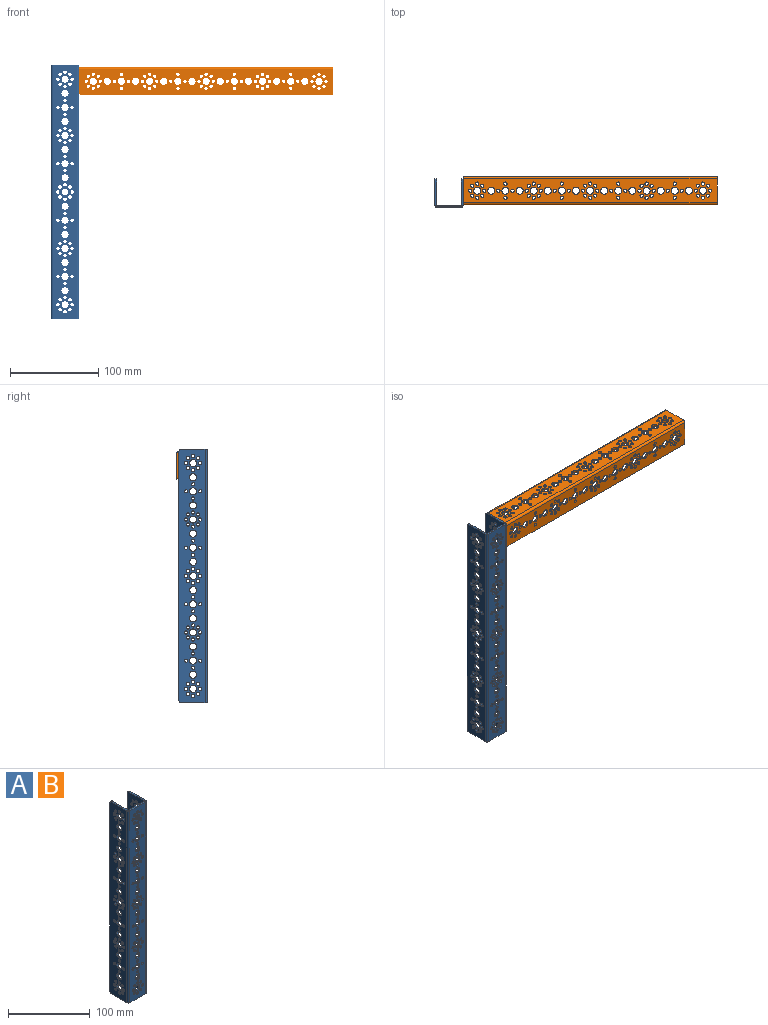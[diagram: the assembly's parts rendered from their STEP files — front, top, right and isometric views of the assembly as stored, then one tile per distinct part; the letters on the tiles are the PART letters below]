
ASSEMBLY  parts=2 mates=1
PART A: 237 faces, bbox 32x32x288 mm
  f0: plane 288x29.5mm, normal (1,0,0), area 7036.7mm2, adj f7,f8,f12,f13,f14,f17,f20,f22
  f1: plane 288x29.5mm, normal (-1,0,0), area 7036.7mm2, adj f8,f9,f12,f13,f14,f17,f20,f22
  f2: plane 288x29.5mm, normal (1,0,0), area 7036.7mm2, adj f10,f11,f12,f13,f15,f16,f19,f21
  f3: plane 288x29.5mm, normal (-1,0,0), area 7036.7mm2, adj f6,f11,f12,f13,f15,f16,f19,f21
  f4: plane 288x27mm, normal (0,-1,0), area 6319.4mm2, adj f6,f7,f12,f13,f18,f23,f24,f25
  f5: plane 288x27mm, normal (0,1,0), area 6319.4mm2, adj f9,f10,f12,f13,f18,f23,f24,f25
  f6: cylinder r=2.5mm len=288mm, axis (0,0,-1), area 1131mm2, adj f3,f4,f12,f13
  f7: cylinder r=2.5mm len=288mm, axis (0,0,-1), area 1131mm2, adj f0,f4,f12,f13
  f8: plane 283x2mm, normal (0,1,0), area 566mm2, adj f0,f1,f14,f17
  f9: cylinder r=0.5mm len=288mm, axis (0,0,-1), area 226.2mm2, adj f1,f5,f12,f13
  f10: cylinder r=0.5mm len=288mm, axis (0,0,-1), area 226.2mm2, adj f2,f5,f12,f13
  f11: plane 283x2mm, normal (0,1,0), area 566mm2, adj f2,f3,f15,f16
  f12: plane 32x29.5mm, normal (0,0,1), area 171.4mm2, adj f0,f1,f2,f3,f4,f5,f6,f7
  f13: plane 32x29.5mm, normal (0,0,-1), area 171.4mm2, adj f0,f1,f2,f3,f4,f5,f6,f7
  f14: cylinder r=2.5mm len=2.5mm, axis (1,0,0), area 7.9mm2, adj f0,f1,f8,f12
  f15: cylinder r=2.5mm len=2.5mm, axis (1,0,0), area 7.9mm2, adj f2,f3,f11,f12
  f16: cylinder r=2.5mm len=2.5mm, axis (-1,0,0), area 7.9mm2, adj f2,f3,f11,f13
  f17: cylinder r=2.5mm len=2.5mm, axis (-1,0,0), area 7.9mm2, adj f0,f1,f8,f13
  f18: cylinder r=4mm len=8mm, axis (0,-1,0), area 50.3mm2, adj f4,f5
  f19: cylinder r=4mm len=8mm, axis (-1,0,0), area 50.3mm2, adj f2,f3
  f20: cylinder r=4mm len=8mm, axis (-1,0,0), area 50.3mm2, adj f0,f1
  f21: cylinder r=1.85mm len=3.7mm, axis (-1,0,0), area 23.2mm2, adj f2,f3
  f22: cylinder r=1.85mm len=3.7mm, axis (-1,0,0), area 23.2mm2, adj f0,f1
  f23: cylinder r=1.85mm len=3.7mm, axis (0,-1,0), area 23.2mm2, adj f4,f5
  f24: cylinder r=4mm len=8mm, axis (0,-1,0), area 50.3mm2, adj f4,f5
  f25: cylinder r=4mm len=8mm, axis (0,-1,0), area 50.3mm2, adj f4,f5
  f26: cylinder r=4mm len=8mm, axis (0,-1,0), area 50.3mm2, adj f4,f5
  f27: cylinder r=4mm len=8mm, axis (0,-1,0), area 50.3mm2, adj f4,f5
  f28: cylinder r=4mm len=8mm, axis (0,-1,0), area 50.3mm2, adj f4,f5
  f29: cylinder r=4mm len=8mm, axis (0,-1,0), area 50.3mm2, adj f4,f5
  f30: cylinder r=4mm len=8mm, axis (0,-1,0), area 50.3mm2, adj f4,f5
  f31: cylinder r=4mm len=8mm, axis (0,-1,0), area 50.3mm2, adj f4,f5
  f32: cylinder r=4mm len=8mm, axis (0,-1,0), area 50.3mm2, adj f4,f5
  f33: cylinder r=4mm len=8mm, axis (0,-1,0), area 50.3mm2, adj f4,f5
  f34: cylinder r=4mm len=8mm, axis (0,-1,0), area 50.3mm2, adj f4,f5
  f35: cylinder r=4mm len=8mm, axis (0,-1,0), area 50.3mm2, adj f4,f5
  f36: cylinder r=4mm len=8mm, axis (0,-1,0), area 50.3mm2, adj f4,f5
  f37: cylinder r=4mm len=8mm, axis (0,-1,0), area 50.3mm2, adj f4,f5
  f38: cylinder r=4mm len=8mm, axis (0,-1,0), area 50.3mm2, adj f4,f5
  f39: cylinder r=4mm len=8mm, axis (0,-1,0), area 50.3mm2, adj f4,f5
  f40: cylinder r=4mm len=8mm, axis (-1,0,0), area 50.3mm2, adj f2,f3
  f41: cylinder r=4mm len=8mm, axis (-1,0,0), area 50.3mm2, adj f0,f1
  f42: cylinder r=4mm len=8mm, axis (-1,0,0), area 50.3mm2, adj f2,f3
  f43: cylinder r=4mm len=8mm, axis (-1,0,0), area 50.3mm2, adj f0,f1
  f44: cylinder r=4mm len=8mm, axis (-1,0,0), area 50.3mm2, adj f2,f3
  f45: cylinder r=4mm len=8mm, axis (-1,0,0), area 50.3mm2, adj f0,f1
  f46: cylinder r=4mm len=8mm, axis (-1,0,0), area 50.3mm2, adj f2,f3
  f47: cylinder r=4mm len=8mm, axis (-1,0,0), area 50.3mm2, adj f0,f1
  f48: cylinder r=4mm len=8mm, axis (-1,0,0), area 50.3mm2, adj f2,f3
  f49: cylinder r=4mm len=8mm, axis (-1,0,0), area 50.3mm2, adj f0,f1
  f50: cylinder r=4mm len=8mm, axis (-1,0,0), area 50.3mm2, adj f2,f3
  f51: cylinder r=4mm len=8mm, axis (-1,0,0), area 50.3mm2, adj f0,f1
  f52: cylinder r=4mm len=8mm, axis (-1,0,0), area 50.3mm2, adj f2,f3
  f53: cylinder r=4mm len=8mm, axis (-1,0,0), area 50.3mm2, adj f0,f1
  f54: cylinder r=4mm len=8mm, axis (-1,0,0), area 50.3mm2, adj f2,f3
  f55: cylinder r=4mm len=8mm, axis (-1,0,0), area 50.3mm2, adj f0,f1
  f56: cylinder r=4mm len=8mm, axis (-1,0,0), area 50.3mm2, adj f2,f3
  f57: cylinder r=4mm len=8mm, axis (-1,0,0), area 50.3mm2, adj f0,f1
  f58: cylinder r=4mm len=8mm, axis (-1,0,0), area 50.3mm2, adj f2,f3
  f59: cylinder r=4mm len=8mm, axis (-1,0,0), area 50.3mm2, adj f0,f1
  f60: cylinder r=4mm len=8mm, axis (-1,0,0), area 50.3mm2, adj f2,f3
  f61: cylinder r=4mm len=8mm, axis (-1,0,0), area 50.3mm2, adj f0,f1
  f62: cylinder r=4mm len=8mm, axis (-1,0,0), area 50.3mm2, adj f2,f3
  f63: cylinder r=4mm len=8mm, axis (-1,0,0), area 50.3mm2, adj f0,f1
  f64: cylinder r=4mm len=8mm, axis (-1,0,0), area 50.3mm2, adj f2,f3
  f65: cylinder r=4mm len=8mm, axis (-1,0,0), area 50.3mm2, adj f0,f1
  f66: cylinder r=4mm len=8mm, axis (-1,0,0), area 50.3mm2, adj f2,f3
  f67: cylinder r=4mm len=8mm, axis (-1,0,0), area 50.3mm2, adj f0,f1
  f68: cylinder r=4mm len=8mm, axis (-1,0,0), area 50.3mm2, adj f2,f3
  f69: cylinder r=4mm len=8mm, axis (-1,0,0), area 50.3mm2, adj f0,f1
  f70: cylinder r=4mm len=8mm, axis (-1,0,0), area 50.3mm2, adj f2,f3
  f71: cylinder r=4mm len=8mm, axis (-1,0,0), area 50.3mm2, adj f0,f1
  f72: cylinder r=1.85mm len=3.7mm, axis (0,-1,0), area 23.2mm2, adj f4,f5
  f73: cylinder r=1.85mm len=3.7mm, axis (0,-1,0), area 23.2mm2, adj f4,f5
  f74: cylinder r=1.85mm len=3.7mm, axis (0,-1,0), area 23.2mm2, adj f4,f5
  f75: cylinder r=1.85mm len=3.7mm, axis (0,-1,0), area 23.2mm2, adj f4,f5
  f76: cylinder r=1.85mm len=3.7mm, axis (0,-1,0), area 23.2mm2, adj f4,f5
  f77: cylinder r=1.85mm len=3.7mm, axis (0,-1,0), area 23.2mm2, adj f4,f5
  f78: cylinder r=1.85mm len=3.7mm, axis (0,-1,0), area 23.2mm2, adj f4,f5
  f79: cylinder r=1.85mm len=3.7mm, axis (-1,0,0), area 23.2mm2, adj f2,f3
  f80: cylinder r=1.85mm len=3.7mm, axis (-1,0,0), area 23.2mm2, adj f0,f1
  f81: cylinder r=1.85mm len=3.7mm, axis (-1,0,0), area 23.2mm2, adj f2,f3
  f82: cylinder r=1.85mm len=3.7mm, axis (-1,0,0), area 23.2mm2, adj f0,f1
  f83: cylinder r=1.85mm len=3.7mm, axis (-1,0,0), area 23.2mm2, adj f2,f3
  f84: cylinder r=1.85mm len=3.7mm, axis (-1,0,0), area 23.2mm2, adj f0,f1
  f85: cylinder r=1.85mm len=3.7mm, axis (-1,0,0), area 23.2mm2, adj f2,f3
  f86: cylinder r=1.85mm len=3.7mm, axis (-1,0,0), area 23.2mm2, adj f0,f1
  f87: cylinder r=1.85mm len=3.7mm, axis (-1,0,0), area 23.2mm2, adj f2,f3
  f88: cylinder r=1.85mm len=3.7mm, axis (-1,0,0), area 23.2mm2, adj f0,f1
  f89: cylinder r=1.85mm len=3.7mm, axis (-1,0,0), area 23.2mm2, adj f2,f3
  f90: cylinder r=1.85mm len=3.7mm, axis (-1,0,0), area 23.2mm2, adj f0,f1
  f91: cylinder r=1.85mm len=3.7mm, axis (-1,0,0), area 23.2mm2, adj f2,f3
  f92: cylinder r=1.85mm len=3.7mm, axis (-1,0,0), area 23.2mm2, adj f0,f1
  f93: cylinder r=1.85mm len=3.7mm, axis (0,-1,0), area 23.2mm2, adj f4,f5
  f94: cylinder r=1.85mm len=3.7mm, axis (-1,0,0), area 23.2mm2, adj f2,f3
  f95: cylinder r=1.85mm len=3.7mm, axis (-1,0,0), area 23.2mm2, adj f0,f1
  f96: cylinder r=1.85mm len=3.7mm, axis (0,-1,0), area 23.2mm2, adj f4,f5
  f97: cylinder r=1.85mm len=3.7mm, axis (0,-1,0), area 23.2mm2, adj f4,f5
  f98: cylinder r=1.85mm len=3.7mm, axis (0,-1,0), area 23.2mm2, adj f4,f5
  f99: cylinder r=1.85mm len=3.7mm, axis (-1,0,0), area 23.2mm2, adj f2,f3
  f100: cylinder r=1.85mm len=3.7mm, axis (-1,0,0), area 23.2mm2, adj f0,f1
  f101: cylinder r=1.85mm len=3.7mm, axis (-1,0,0), area 23.2mm2, adj f2,f3
  f102: cylinder r=1.85mm len=3.7mm, axis (-1,0,0), area 23.2mm2, adj f0,f1
  f103: cylinder r=1.85mm len=3.7mm, axis (-1,0,0), area 23.2mm2, adj f2,f3
  f104: cylinder r=1.85mm len=3.7mm, axis (-1,0,0), area 23.2mm2, adj f0,f1
  f105: cylinder r=1.85mm len=3.7mm, axis (0,-1,0), area 23.2mm2, adj f4,f5
  f106: cylinder r=1.85mm len=3.7mm, axis (0,-1,0), area 23.2mm2, adj f4,f5
  f107: cylinder r=1.85mm len=3.7mm, axis (0,-1,0), area 23.2mm2, adj f4,f5
  f108: cylinder r=1.85mm len=3.7mm, axis (0,-1,0), area 23.2mm2, adj f4,f5
  f109: cylinder r=1.85mm len=3.7mm, axis (0,-1,0), area 23.2mm2, adj f4,f5
  f110: cylinder r=1.85mm len=3.7mm, axis (0,-1,0), area 23.2mm2, adj f4,f5
  f111: cylinder r=1.85mm len=3.7mm, axis (0,-1,0), area 23.2mm2, adj f4,f5
  f112: cylinder r=1.85mm len=3.7mm, axis (0,-1,0), area 23.2mm2, adj f4,f5
  f113: cylinder r=1.85mm len=3.7mm, axis (0,-1,0), area 23.2mm2, adj f4,f5
  f114: cylinder r=1.85mm len=3.7mm, axis (0,-1,0), area 23.2mm2, adj f4,f5
  f115: cylinder r=1.85mm len=3.7mm, axis (0,-1,0), area 23.2mm2, adj f4,f5
  f116: cylinder r=1.85mm len=3.7mm, axis (0,-1,0), area 23.2mm2, adj f4,f5
  f117: cylinder r=1.85mm len=3.7mm, axis (0,-1,0), area 23.2mm2, adj f4,f5
  f118: cylinder r=1.85mm len=3.7mm, axis (0,-1,0), area 23.2mm2, adj f4,f5
  f119: cylinder r=1.85mm len=3.7mm, axis (0,-1,0), area 23.2mm2, adj f4,f5
  f120: cylinder r=1.85mm len=3.7mm, axis (0,-1,0), area 23.2mm2, adj f4,f5
  f121: cylinder r=1.85mm len=3.7mm, axis (-1,0,0), area 23.2mm2, adj f2,f3
  f122: cylinder r=1.85mm len=3.7mm, axis (-1,0,0), area 23.2mm2, adj f0,f1
  f123: cylinder r=1.85mm len=3.7mm, axis (-1,0,0), area 23.2mm2, adj f2,f3
  f124: cylinder r=1.85mm len=3.7mm, axis (-1,0,0), area 23.2mm2, adj f0,f1
  f125: cylinder r=1.85mm len=3.7mm, axis (-1,0,0), area 23.2mm2, adj f2,f3
  f126: cylinder r=1.85mm len=3.7mm, axis (-1,0,0), area 23.2mm2, adj f0,f1
  f127: cylinder r=1.85mm len=3.7mm, axis (-1,0,0), area 23.2mm2, adj f2,f3
  f128: cylinder r=1.85mm len=3.7mm, axis (-1,0,0), area 23.2mm2, adj f0,f1
  f129: cylinder r=1.85mm len=3.7mm, axis (-1,0,0), area 23.2mm2, adj f2,f3
  f130: cylinder r=1.85mm len=3.7mm, axis (-1,0,0), area 23.2mm2, adj f0,f1
  f131: cylinder r=1.85mm len=3.7mm, axis (-1,0,0), area 23.2mm2, adj f2,f3
  f132: cylinder r=1.85mm len=3.7mm, axis (-1,0,0), area 23.2mm2, adj f0,f1
  f133: cylinder r=1.85mm len=3.7mm, axis (-1,0,0), area 23.2mm2, adj f2,f3
  f134: cylinder r=1.85mm len=3.7mm, axis (-1,0,0), area 23.2mm2, adj f0,f1
  f135: cylinder r=1.85mm len=3.7mm, axis (-1,0,0), area 23.2mm2, adj f2,f3
  f136: cylinder r=1.85mm len=3.7mm, axis (-1,0,0), area 23.2mm2, adj f0,f1
  f137: cylinder r=1.85mm len=3.7mm, axis (-1,0,0), area 23.2mm2, adj f2,f3
  f138: cylinder r=1.85mm len=3.7mm, axis (-1,0,0), area 23.2mm2, adj f0,f1
  f139: cylinder r=1.85mm len=3.7mm, axis (-1,0,0), area 23.2mm2, adj f2,f3
  f140: cylinder r=1.85mm len=3.7mm, axis (-1,0,0), area 23.2mm2, adj f0,f1
  f141: cylinder r=1.85mm len=3.7mm, axis (-1,0,0), area 23.2mm2, adj f2,f3
  f142: cylinder r=1.85mm len=3.7mm, axis (-1,0,0), area 23.2mm2, adj f0,f1
  f143: cylinder r=1.85mm len=3.7mm, axis (-1,0,0), area 23.2mm2, adj f2,f3
  f144: cylinder r=1.85mm len=3.7mm, axis (-1,0,0), area 23.2mm2, adj f0,f1
  f145: cylinder r=1.85mm len=3.7mm, axis (-1,0,0), area 23.2mm2, adj f2,f3
  f146: cylinder r=1.85mm len=3.7mm, axis (-1,0,0), area 23.2mm2, adj f0,f1
  f147: cylinder r=1.85mm len=3.7mm, axis (-1,0,0), area 23.2mm2, adj f2,f3
  f148: cylinder r=1.85mm len=3.7mm, axis (-1,0,0), area 23.2mm2, adj f0,f1
  f149: cylinder r=1.85mm len=3.7mm, axis (-1,0,0), area 23.2mm2, adj f2,f3
  f150: cylinder r=1.85mm len=3.7mm, axis (-1,0,0), area 23.2mm2, adj f0,f1
  f151: cylinder r=1.85mm len=3.7mm, axis (-1,0,0), area 23.2mm2, adj f2,f3
  f152: cylinder r=1.85mm len=3.7mm, axis (-1,0,0), area 23.2mm2, adj f0,f1
  f153: cylinder r=1.85mm len=3.7mm, axis (0,-1,0), area 23.2mm2, adj f4,f5
  f154: cylinder r=1.85mm len=3.7mm, axis (0,-1,0), area 23.2mm2, adj f4,f5
  f155: cylinder r=1.85mm len=3.7mm, axis (0,-1,0), area 23.2mm2, adj f4,f5
  f156: cylinder r=1.85mm len=3.7mm, axis (0,-1,0), area 23.2mm2, adj f4,f5
  f157: cylinder r=1.85mm len=3.7mm, axis (-1,0,0), area 23.2mm2, adj f2,f3
  f158: cylinder r=1.85mm len=3.7mm, axis (-1,0,0), area 23.2mm2, adj f0,f1
  f159: cylinder r=1.85mm len=3.7mm, axis (-1,0,0), area 23.2mm2, adj f2,f3
  f160: cylinder r=1.85mm len=3.7mm, axis (-1,0,0), area 23.2mm2, adj f0,f1
  f161: cylinder r=1.85mm len=3.7mm, axis (-1,0,0), area 23.2mm2, adj f2,f3
  f162: cylinder r=1.85mm len=3.7mm, axis (-1,0,0), area 23.2mm2, adj f0,f1
  f163: cylinder r=1.85mm len=3.7mm, axis (-1,0,0), area 23.2mm2, adj f2,f3
  f164: cylinder r=1.85mm len=3.7mm, axis (-1,0,0), area 23.2mm2, adj f0,f1
  f165: cylinder r=1.85mm len=3.7mm, axis (0,-1,0), area 23.2mm2, adj f4,f5
  f166: cylinder r=1.85mm len=3.7mm, axis (0,-1,0), area 23.2mm2, adj f4,f5
  f167: cylinder r=1.85mm len=3.7mm, axis (0,-1,0), area 23.2mm2, adj f4,f5
  f168: cylinder r=1.85mm len=3.7mm, axis (0,-1,0), area 23.2mm2, adj f4,f5
  f169: cylinder r=1.85mm len=3.7mm, axis (0,-1,0), area 23.2mm2, adj f4,f5
  f170: cylinder r=1.85mm len=3.7mm, axis (0,-1,0), area 23.2mm2, adj f4,f5
  f171: cylinder r=1.85mm len=3.7mm, axis (0,-1,0), area 23.2mm2, adj f4,f5
  f172: cylinder r=1.85mm len=3.7mm, axis (0,-1,0), area 23.2mm2, adj f4,f5
  f173: cylinder r=1.85mm len=3.7mm, axis (0,-1,0), area 23.2mm2, adj f4,f5
  f174: cylinder r=1.85mm len=3.7mm, axis (0,-1,0), area 23.2mm2, adj f4,f5
  f175: cylinder r=1.85mm len=3.7mm, axis (0,-1,0), area 23.2mm2, adj f4,f5
  f176: cylinder r=1.85mm len=3.7mm, axis (0,-1,0), area 23.2mm2, adj f4,f5
  f177: cylinder r=1.85mm len=3.7mm, axis (0,-1,0), area 23.2mm2, adj f4,f5
  f178: cylinder r=1.85mm len=3.7mm, axis (0,-1,0), area 23.2mm2, adj f4,f5
  f179: cylinder r=1.85mm len=3.7mm, axis (0,-1,0), area 23.2mm2, adj f4,f5
  f180: cylinder r=1.85mm len=3.7mm, axis (0,-1,0), area 23.2mm2, adj f4,f5
  f181: cylinder r=1.85mm len=3.7mm, axis (-1,0,0), area 23.2mm2, adj f2,f3
  f182: cylinder r=1.85mm len=3.7mm, axis (-1,0,0), area 23.2mm2, adj f0,f1
  f183: cylinder r=1.85mm len=3.7mm, axis (-1,0,0), area 23.2mm2, adj f2,f3
  f184: cylinder r=1.85mm len=3.7mm, axis (-1,0,0), area 23.2mm2, adj f0,f1
  f185: cylinder r=1.85mm len=3.7mm, axis (-1,0,0), area 23.2mm2, adj f2,f3
  f186: cylinder r=1.85mm len=3.7mm, axis (-1,0,0), area 23.2mm2, adj f0,f1
  f187: cylinder r=1.85mm len=3.7mm, axis (-1,0,0), area 23.2mm2, adj f2,f3
  f188: cylinder r=1.85mm len=3.7mm, axis (-1,0,0), area 23.2mm2, adj f0,f1
  f189: cylinder r=1.85mm len=3.7mm, axis (-1,0,0), area 23.2mm2, adj f2,f3
  f190: cylinder r=1.85mm len=3.7mm, axis (-1,0,0), area 23.2mm2, adj f0,f1
  f191: cylinder r=1.85mm len=3.7mm, axis (-1,0,0), area 23.2mm2, adj f2,f3
  f192: cylinder r=1.85mm len=3.7mm, axis (-1,0,0), area 23.2mm2, adj f0,f1
  f193: cylinder r=1.85mm len=3.7mm, axis (-1,0,0), area 23.2mm2, adj f2,f3
  f194: cylinder r=1.85mm len=3.7mm, axis (-1,0,0), area 23.2mm2, adj f0,f1
  f195: cylinder r=1.85mm len=3.7mm, axis (-1,0,0), area 23.2mm2, adj f2,f3
  f196: cylinder r=1.85mm len=3.7mm, axis (-1,0,0), area 23.2mm2, adj f0,f1
  f197: cylinder r=1.85mm len=3.7mm, axis (-1,0,0), area 23.2mm2, adj f2,f3
  f198: cylinder r=1.85mm len=3.7mm, axis (-1,0,0), area 23.2mm2, adj f0,f1
  f199: cylinder r=1.85mm len=3.7mm, axis (-1,0,0), area 23.2mm2, adj f2,f3
  f200: cylinder r=1.85mm len=3.7mm, axis (-1,0,0), area 23.2mm2, adj f0,f1
  f201: cylinder r=1.85mm len=3.7mm, axis (-1,0,0), area 23.2mm2, adj f2,f3
  f202: cylinder r=1.85mm len=3.7mm, axis (-1,0,0), area 23.2mm2, adj f0,f1
  f203: cylinder r=1.85mm len=3.7mm, axis (-1,0,0), area 23.2mm2, adj f2,f3
  f204: cylinder r=1.85mm len=3.7mm, axis (-1,0,0), area 23.2mm2, adj f0,f1
  f205: cylinder r=1.85mm len=3.7mm, axis (-1,0,0), area 23.2mm2, adj f2,f3
  f206: cylinder r=1.85mm len=3.7mm, axis (-1,0,0), area 23.2mm2, adj f0,f1
  f207: cylinder r=1.85mm len=3.7mm, axis (-1,0,0), area 23.2mm2, adj f2,f3
  f208: cylinder r=1.85mm len=3.7mm, axis (-1,0,0), area 23.2mm2, adj f0,f1
  f209: cylinder r=1.85mm len=3.7mm, axis (-1,0,0), area 23.2mm2, adj f2,f3
  f210: cylinder r=1.85mm len=3.7mm, axis (-1,0,0), area 23.2mm2, adj f0,f1
  f211: cylinder r=1.85mm len=3.7mm, axis (-1,0,0), area 23.2mm2, adj f2,f3
  f212: cylinder r=1.85mm len=3.7mm, axis (-1,0,0), area 23.2mm2, adj f0,f1
  f213: cylinder r=1.85mm len=3.7mm, axis (0,-1,0), area 23.2mm2, adj f4,f5
  f214: cylinder r=1.85mm len=3.7mm, axis (0,-1,0), area 23.2mm2, adj f4,f5
  f215: cylinder r=1.85mm len=3.7mm, axis (0,-1,0), area 23.2mm2, adj f4,f5
  f216: cylinder r=1.85mm len=3.7mm, axis (0,-1,0), area 23.2mm2, adj f4,f5
  f217: cylinder r=1.85mm len=3.7mm, axis (0,-1,0), area 23.2mm2, adj f4,f5
  f218: cylinder r=1.85mm len=3.7mm, axis (0,-1,0), area 23.2mm2, adj f4,f5
  f219: cylinder r=1.85mm len=3.7mm, axis (0,-1,0), area 23.2mm2, adj f4,f5
  f220: cylinder r=1.85mm len=3.7mm, axis (0,-1,0), area 23.2mm2, adj f4,f5
  f221: cylinder r=1.85mm len=3.7mm, axis (-1,0,0), area 23.2mm2, adj f2,f3
  f222: cylinder r=1.85mm len=3.7mm, axis (-1,0,0), area 23.2mm2, adj f0,f1
  f223: cylinder r=1.85mm len=3.7mm, axis (-1,0,0), area 23.2mm2, adj f2,f3
  f224: cylinder r=1.85mm len=3.7mm, axis (-1,0,0), area 23.2mm2, adj f0,f1
  f225: cylinder r=1.85mm len=3.7mm, axis (-1,0,0), area 23.2mm2, adj f2,f3
  f226: cylinder r=1.85mm len=3.7mm, axis (-1,0,0), area 23.2mm2, adj f0,f1
  f227: cylinder r=1.85mm len=3.7mm, axis (-1,0,0), area 23.2mm2, adj f2,f3
  f228: cylinder r=1.85mm len=3.7mm, axis (-1,0,0), area 23.2mm2, adj f0,f1
  f229: cylinder r=1.85mm len=3.7mm, axis (-1,0,0), area 23.2mm2, adj f2,f3
  f230: cylinder r=1.85mm len=3.7mm, axis (-1,0,0), area 23.2mm2, adj f0,f1
  f231: cylinder r=1.85mm len=3.7mm, axis (-1,0,0), area 23.2mm2, adj f2,f3
  f232: cylinder r=1.85mm len=3.7mm, axis (-1,0,0), area 23.2mm2, adj f0,f1
  f233: cylinder r=1.85mm len=3.7mm, axis (-1,0,0), area 23.2mm2, adj f2,f3
  f234: cylinder r=1.85mm len=3.7mm, axis (-1,0,0), area 23.2mm2, adj f0,f1
  f235: cylinder r=1.85mm len=3.7mm, axis (-1,0,0), area 23.2mm2, adj f2,f3
  f236: cylinder r=1.85mm len=3.7mm, axis (-1,0,0), area 23.2mm2, adj f0,f1
PART B: same geometry as A
PLACE A t=(15.6,-42.62,74.3)mm
PLACE B rot(axis=(-0.58,-0.58,0.58),120deg) t=(175.6,-24.12,215.8)mm
MATE revolute A.f0 <-> B.f12  axis (1,0,0) through (31.6,-10.62,215.8)mm
